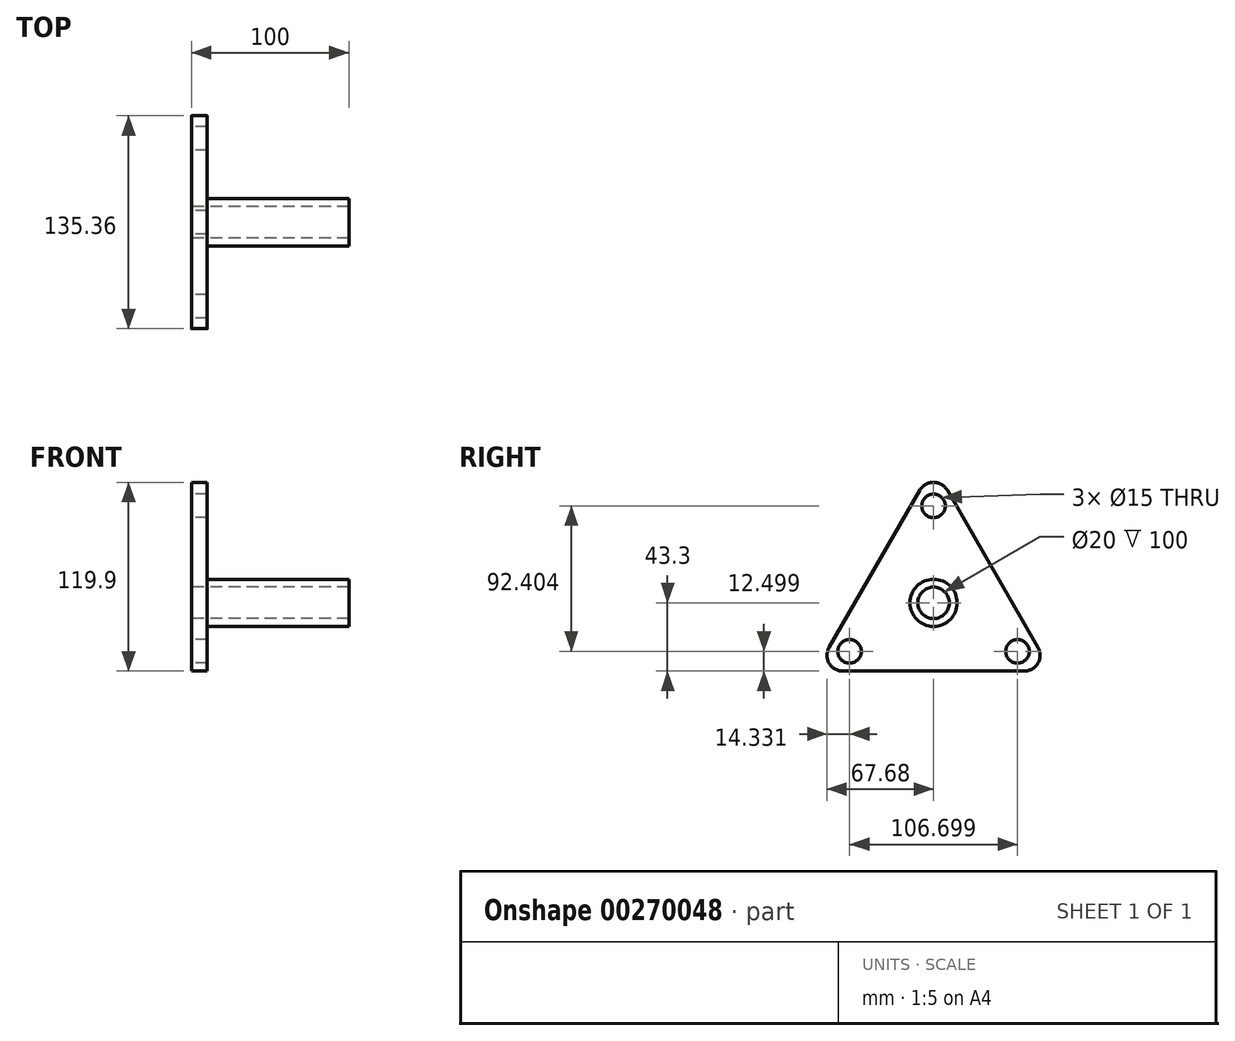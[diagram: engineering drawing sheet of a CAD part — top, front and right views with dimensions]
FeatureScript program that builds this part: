
annotation { "Feature Type Name" : "Feature", "Feature Type Description" : "" }
export const myFeature = defineFeature(function(context is Context, id is Id, definition is map)
    precondition{}
    {
        {
            var Q0;
            Q0=qCreatedBy(makeId("Right.planeOp"),FACE);
            var sketch = newSketch(context, id + "F0", { "sketchPlane" : qUnion([Q0])});
            skCircle(sketch, "E0", {"center": v(0, 0) * mm, "radius": 10 * mm});
            skCircle(sketch, "E1", {"center": v(0, 0) * mm, "radius": 15 * mm});
            skSolve(sketch);
        }
        {
            var Q0;
            Q0=makeQuery(id+"F0.imprint","IMPRINT",FACE,{"disambiguationData":[TD([[makeQuery(id+"F0.imprint","IMPRINT",EDGE,{"derivedFrom":sQuery(id+"F0.wireOp",EDGE,"E0")}),-1.0]])]});
            extrude(context, id + "F1", {"entities" : qUnion([Q0]), "depth" : 100 * mm});
        }
        {
            var Q0;
            Q0=qCreatedBy(makeId("Right.planeOp"),FACE);
            var sketch = newSketch(context, id + "F2", { "sketchPlane" : qUnion([Q0])});
            skLineSegment(sketch, "E2", {"start": v(0, 0) * mm, "end": v(-75, -43.3) * mm});
            skLineSegment(sketch, "E3", {"start": v(-75, -43.3) * mm, "end": v(0, 86.6) * mm});
            skLineSegment(sketch, "E4", {"start": v(0, 86.6) * mm, "end": v(75, -43.3) * mm});
            skLineSegment(sketch, "E5", {"start": v(75, -43.3) * mm, "end": v(-75, -43.3) * mm});
            skSolve(sketch);
        }
        {
            var Q0;
            Q0=makeQuery(id+"F2.imprint","IMPRINT",FACE,{"disambiguationData":[TD([[makeQuery(id+"F2.imprint","IMPRINT",EDGE,{"derivedFrom":sQuery(id+"F2.wireOp",EDGE,"E3")}),-1.0]])]});
            extrude(context, id + "F3", {"entities" : qUnion([Q0]), "operationType" : NewBodyOperationType.ADD, "depth" : 10 * mm});
        }
        {
            var Q0;
            Q0=makeQuery(id+"F3.opExtrude","SWEPT_EDGE",EDGE,{"disambiguationData":[OSD([sQuery(id+"F2.wireOp",EDGE,"E3"),sQuery(id+"F2.wireOp",EDGE,"E4")])]});
            var Q1;
            Q1=makeQuery(id+"F3.opExtrude","SWEPT_EDGE",EDGE,{"disambiguationData":[OSD([sQuery(id+"F2.wireOp",EDGE,"E4"),sQuery(id+"F2.wireOp",EDGE,"E5")])]});
            var Q2;
            Q2=makeQuery(id+"F3.opExtrude","SWEPT_EDGE",EDGE,{"disambiguationData":[OSD([sQuery(id+"F2.wireOp",EDGE,"E3"),sQuery(id+"F2.wireOp",EDGE,"E5")])]});
            fillet(context, id + "F4", {"entities" : qUnion([Q0, Q1, Q2]), "radius" : 10 * mm, "tangentPropagation" : true, "allowEdgeOverflow" : false});
        }
        {
            var Q0;
            Q0=qCreatedBy(makeId("Right.planeOp"),FACE);
            var sketch = newSketch(context, id + "F5", { "sketchPlane" : qUnion([Q0])});
            skCircle(sketch, "E6", {"center": v(0, 61.6) * mm, "radius": 7.5 * mm});
            skCircle(sketch, "E7", {"center": v(53.35, -30.8) * mm, "radius": 7.5 * mm});
            skCircle(sketch, "E8", {"center": v(-53.35, -30.8) * mm, "radius": 7.5 * mm});
            skCircle(sketch, "E9", {"center": v(0, 0) * mm, "radius": 10 * mm});
            skSolve(sketch);
        }
        {
            var Q0;
            Q0=makeQuery(id+"F5.imprint","IMPRINT",FACE,{"disambiguationData":[TD([[makeQuery(id+"F5.imprint","IMPRINT",EDGE,{"derivedFrom":sQuery(id+"F5.wireOp",EDGE,"E6")}),1.0]])]});
            var Q1;
            Q1=makeQuery(id+"F5.imprint","IMPRINT",FACE,{"disambiguationData":[TD([[makeQuery(id+"F5.imprint","IMPRINT",EDGE,{"derivedFrom":sQuery(id+"F5.wireOp",EDGE,"E7")}),1.0]])]});
            var Q2;
            Q2=makeQuery(id+"F5.imprint","IMPRINT",FACE,{"disambiguationData":[TD([[makeQuery(id+"F5.imprint","IMPRINT",EDGE,{"derivedFrom":sQuery(id+"F5.wireOp",EDGE,"E8")}),1.0]])]});
            var Q3;
            Q3=makeQuery(id+"F5.imprint","IMPRINT",FACE,{"disambiguationData":[TD([[makeQuery(id+"F5.imprint","IMPRINT",EDGE,{"derivedFrom":sQuery(id+"F5.wireOp",EDGE,"E9")}),1.0]])]});
            extrude(context, id + "F6", {"entities" : qUnion([Q0, Q1, Q2, Q3]), "operationType" : NewBodyOperationType.REMOVE, "endBound" : BoundingType.THROUGH_ALL, "depth" : 25 * mm});
        }
    });
